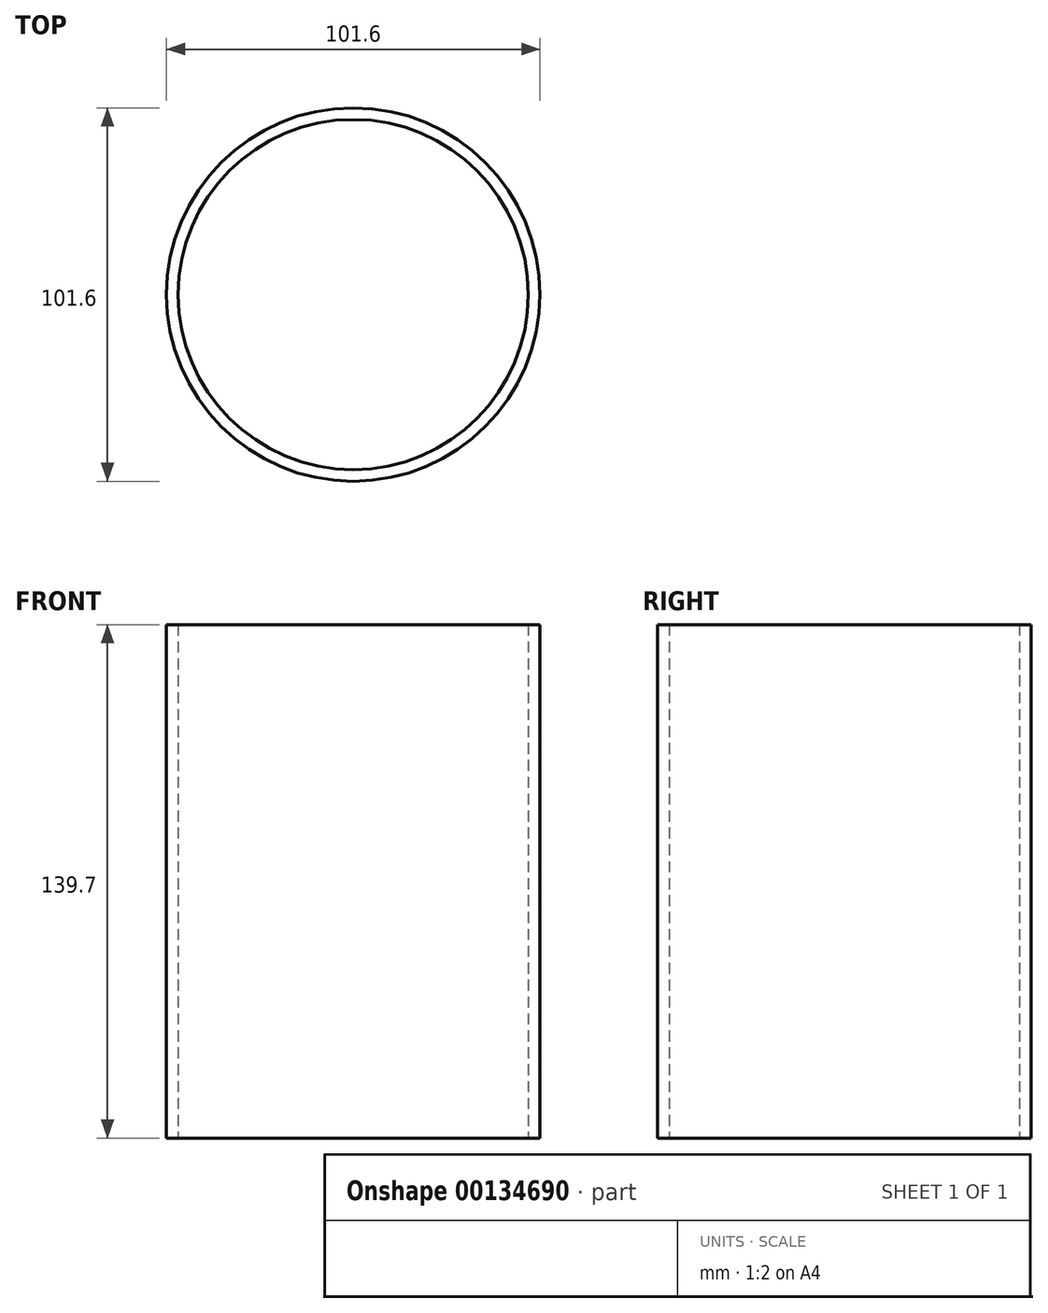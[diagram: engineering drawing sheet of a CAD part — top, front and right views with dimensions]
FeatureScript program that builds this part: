
annotation { "Feature Type Name" : "Feature", "Feature Type Description" : "" }
export const myFeature = defineFeature(function(context is Context, id is Id, definition is map)
    precondition{}
    {
        {
            var Q0;
            Q0=qCreatedBy(makeId("Top.planeOp"),FACE);
            var sketch = newSketch(context, id + "F0", { "sketchPlane" : qUnion([Q0])});
            skCircle(sketch, "E0", {"center": v(0, 0) * mm, "radius": 50.8 * mm});
            skCircle(sketch, "E1", {"center": v(0, 0) * mm, "radius": 47.63 * mm});
            skSolve(sketch);
        }
        {
            var Q0;
            Q0=makeQuery(id+"F0.imprint","IMPRINT",FACE,{"disambiguationData":[TD([[makeQuery(id+"F0.imprint","IMPRINT",EDGE,{"derivedFrom":sQuery(id+"F0.wireOp",EDGE,"E0")}),1.0]])]});
            extrude(context, id + "F1", {"entities" : qUnion([Q0]), "depth" : 139.7 * mm});
        }
    });
